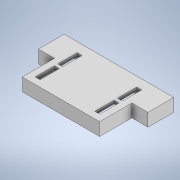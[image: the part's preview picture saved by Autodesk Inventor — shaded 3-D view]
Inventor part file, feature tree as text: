
AUTODESK INVENTOR PART (.ipt)
format: ipt  version: 2021 (Build 250183000, 183)  size: 164,352 bytes
history: native  units: in
note: dims shown in document units (in); Inventor stores cm internally (conversion verified against a paired STEP export)
features: extrude x3, sketch x3, projected_geometry x1
ambient origin geometry x8: Origin, YZ Plane, XZ Plane, XY Plane, X Axis, Y Axis, Z Axis, Center Point
bodies: Solid1 (feature_tree)
feature tree (7):
  extrude  "Extrusion1"  Depth=0.315in
  extrude  "Extrusion2"  Depth=0.2362in
  extrude  "Extrusion3"  Depth=0.3937in
  sketch  "Sketch1"  dims[d0=1.3386in d1=0.315in]
  sketch  "Sketch2"  dims[d4=1.2598in d5=0.2362in]
  sketch  "Sketch3"  dims[d9=0.9449in d17=0.3937in d18=0.8661in d19=0.1181in d20=0.0in d21=0.0394in d22=0.0in d23=0.0394in d24=0.0394in d26=0.0591in d27=0.2362in d28=0.0394in d29=0.0591in d30=0.2362in d31=0.0394in d32=0.0394in d33=0.0591in d34=0.2362in d35=0.0394in d36=0.0394in d37=0.0in]
  projected_geometry  "Projected Loop1"
